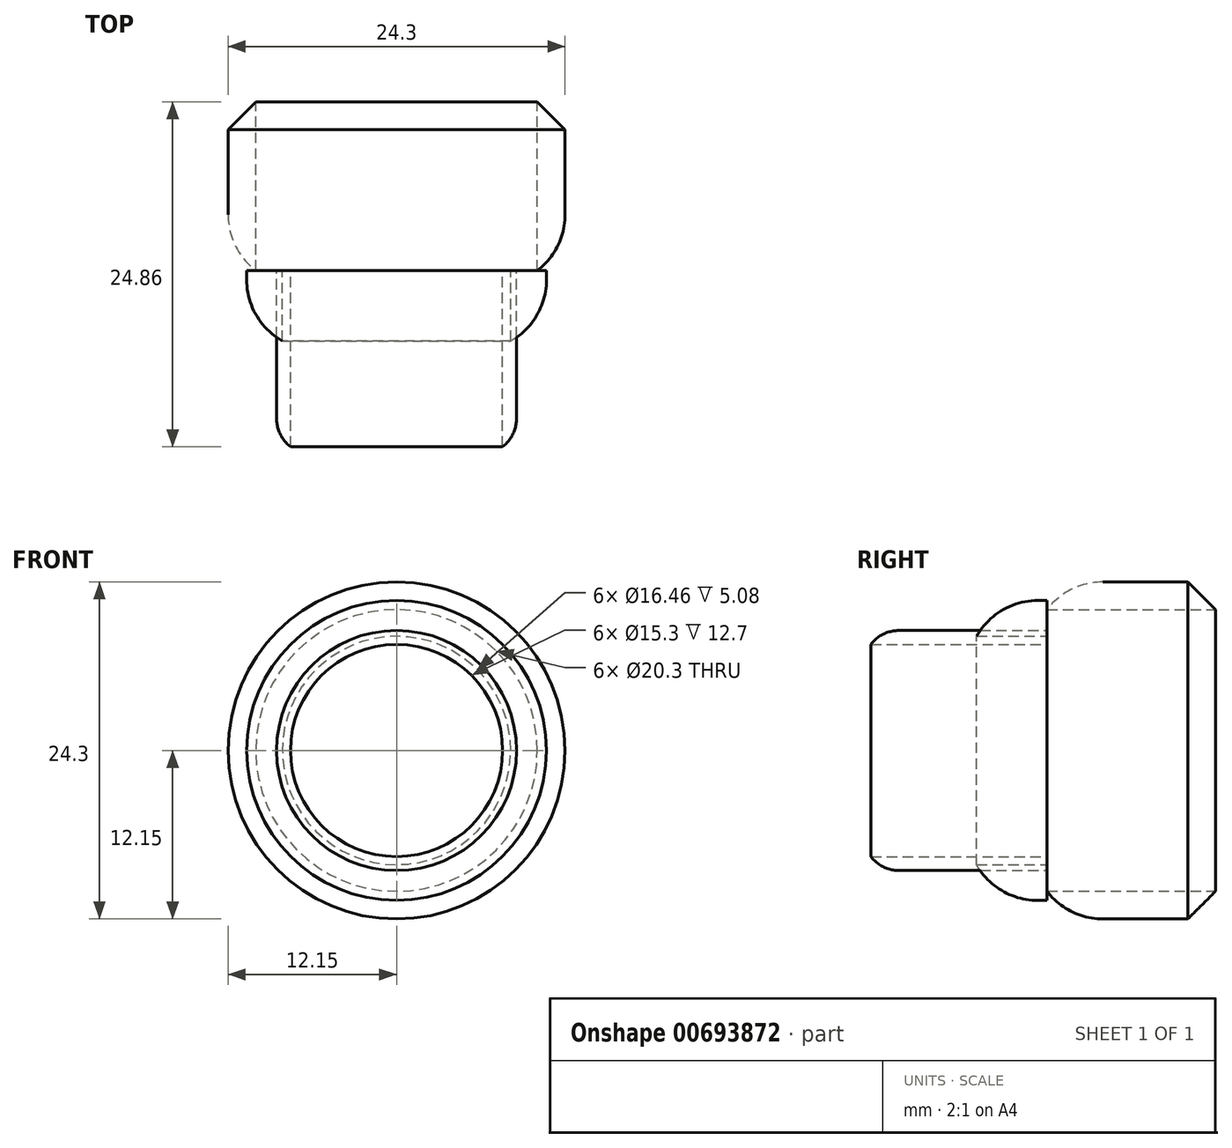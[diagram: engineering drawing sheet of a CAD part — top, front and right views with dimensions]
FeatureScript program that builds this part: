
annotation { "Feature Type Name" : "Feature", "Feature Type Description" : "" }
export const myFeature = defineFeature(function(context is Context, id is Id, definition is map)
    precondition{}
    {
        {
            var Q0;
            Q0=qCreatedBy(makeId("Front.planeOp"),FACE);
            var sketch = newSketch(context, id + "F0", { "sketchPlane" : qUnion([Q0])});
            skCircle(sketch, "E0", {"center": v(0, 0) * mm, "radius": 10.15 * mm});
            skCircle(sketch, "E1", {"center": v(0, 0) * mm, "radius": 12.15 * mm});
            skSolve(sketch);
        }
        {
            var Q0;
            Q0=makeQuery(id+"F0.imprint","IMPRINT",FACE,{"disambiguationData":[TD([[makeQuery(id+"F0.imprint","IMPRINT",EDGE,{"derivedFrom":sQuery(id+"F0.wireOp",EDGE,"E0")}),-1.0]])]});
            extrude(context, id + "F1", {"entities" : qUnion([Q0]), "depth" : 15.24 * mm, "offsetDistance" : 25.4 * mm});
        }
        {
            var Q0;
            Q0=makeQuery(id+"F1.opExtrude","CAP_FACE",FACE,{"disambiguationData":[OSD([sQuery(id+"F0.wireOp",EDGE,"E0"),sQuery(id+"F0.wireOp",EDGE,"E1")])],"isStart":false});
            var sketch = newSketch(context, id + "F2", { "sketchPlane" : qUnion([Q0])});
            skCircle(sketch, "E2", {"center": v(0, 0) * mm, "radius": 8.65 * mm});
            skCircle(sketch, "E3", {"center": v(0, 0) * mm, "radius": 7.65 * mm});
            skSolve(sketch);
        }
        {
            var Q0;
            Q0=makeQuery(id+"F2.imprint","IMPRINT",FACE,{"disambiguationData":[TD([[makeQuery(id+"F2.imprint","IMPRINT",EDGE,{"derivedFrom":sQuery(id+"F2.wireOp",EDGE,"E2")}),1.0]])]});
            extrude(context, id + "F3", {"entities" : qUnion([Q0]), "depth" : 12.7 * mm, "offsetDistance" : 25.4 * mm});
        }
        {
            var Q0;
            Q0=makeQuery(id+"F1.opExtrude","CAP_FACE",FACE,{"disambiguationData":[OSD([sQuery(id+"F0.wireOp",EDGE,"E0"),sQuery(id+"F0.wireOp",EDGE,"E1")])],"isStart":false});
            var sketch = newSketch(context, id + "F4", { "sketchPlane" : qUnion([Q0])});
            skCircle(sketch, "E4", {"center": v(0, 0) * mm, "radius": 10.81 * mm});
            skCircle(sketch, "E5", {"center": v(0, 0) * mm, "radius": 8.23 * mm});
            skSolve(sketch);
        }
        {
            var Q0;
            Q0 = qSketchRegion(id + "F4", true);
            extrude(context, id + "F5", {"entities" : qUnion([Q0]), "depth" : 5.08 * mm, "offsetDistance" : 25.4 * mm});
        }
        {
            var Q0;
            Q0=makeQuery(id+"F1.opExtrude","CAP_EDGE",EDGE,{"disambiguationData":[OSD([sQuery(id+"F0.wireOp",EDGE,"E1")])],"isStart":false});
            fillet(context, id + "F6", {"entities" : qUnion([Q0]), "radius" : 5.08 * mm, "tangentPropagation" : true, "allowEdgeOverflow" : false});
        }
        {
            var Q0;
            Q0=makeQuery(id+"F5.opExtrude","CAP_EDGE",EDGE,{"disambiguationData":[OSD([sQuery(id+"F4.wireOp",EDGE,"E4")])],"isStart":false});
            fillet(context, id + "F7", {"entities" : qUnion([Q0]), "radius" : 5.08 * mm, "tangentPropagation" : true, "allowEdgeOverflow" : false});
        }
        {
            var Q0;
            Q0=makeQuery(id+"F3.opExtrude","CAP_EDGE",EDGE,{"disambiguationData":[OSD([sQuery(id+"F2.wireOp",EDGE,"E2")])],"isStart":false});
            fillet(context, id + "F8", {"entities" : qUnion([Q0]), "radius" : 2.54 * mm, "tangentPropagation" : true, "allowEdgeOverflow" : false});
        }
        {
            var Q0;
            Q0=makeQuery(id+"F1.opExtrude","CAP_EDGE",EDGE,{"disambiguationData":[OSD([sQuery(id+"F0.wireOp",EDGE,"E1")])],"isStart":true});
            chamfer(context, id + "F9", {"entities" : qUnion([Q0]), "width" : 5.08 * mm, "tangentPropagation" : true});
        }
    });
